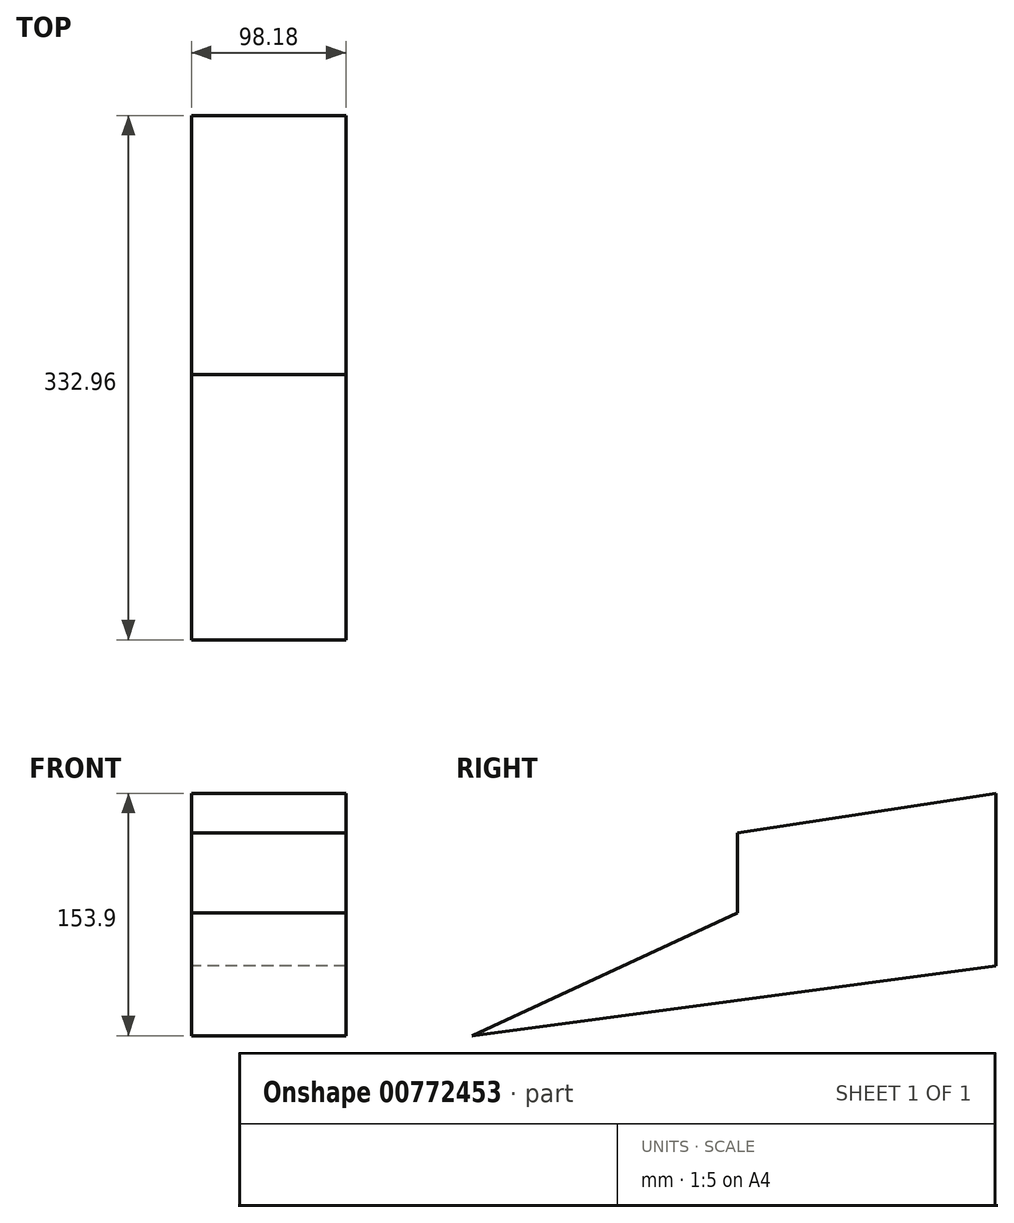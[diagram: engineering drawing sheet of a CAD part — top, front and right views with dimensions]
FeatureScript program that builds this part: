
annotation { "Feature Type Name" : "Feature", "Feature Type Description" : "" }
export const myFeature = defineFeature(function(context is Context, id is Id, definition is map)
    precondition{}
    {
        {
            var Q0;
            Q0=qCreatedBy(makeId("Right.planeOp"),FACE);
            var sketch = newSketch(context, id + "F0", { "sketchPlane" : qUnion([Q0])});
            skLineSegment(sketch, "E0", {"start": v(0, 50.68) * mm, "end": v(164.29, 75.88) * mm});
            skLineSegment(sketch, "E1", {"start": v(164.29, 75.88) * mm, "end": v(164.29, -33.77) * mm});
            skLineSegment(sketch, "E2", {"start": v(164.29, -33.77) * mm, "end": v(-168.67, -78.02) * mm});
            skLineSegment(sketch, "E3", {"start": v(-168.67, -78.02) * mm, "end": v(0, 0) * mm});
            skLineSegment(sketch, "E4", {"start": v(0, 0) * mm, "end": v(0, 50.68) * mm});
            skSolve(sketch);
        }
        {
            var Q0;
            Q0=makeQuery(id+"F0.imprint","IMPRINT",FACE,{"disambiguationData":[TD([[makeQuery(id+"F0.imprint","IMPRINT",EDGE,{"derivedFrom":sQuery(id+"F0.wireOp",EDGE,"E0")}),-1.0]])]});
            extrude(context, id + "F1", {"entities" : qUnion([Q0]), "depth" : 98.18 * mm, "offsetDistance" : 25.4 * mm});
        }
    });
